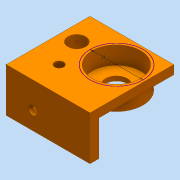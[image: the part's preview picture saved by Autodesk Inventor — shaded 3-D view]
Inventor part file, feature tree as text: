
AUTODESK INVENTOR PART (.ipt)
format: ipt  version: 2016 (Build 200138000, 138)  size: 199,680 bytes
history: native  units: mm
features: extrude x6, sketch x6, hole x5, thicken_offset x2
ambient origin geometry x8: Origin, YZ Plane, XZ Plane, XY Plane, X Axis, Y Axis, Z Axis, Center Point
bodies: Solid1 (feature_tree)
feature tree (19):
  extrude  "Extrusion1"  Depth=20.0mm
  extrude  "Extrusion2"  Depth=16.0mm TaperAngle=0.0deg
  hole  "Hole2"  [1 undecoded]
  hole  "Hole3"  [1 undecoded]
  hole  "Hole4"  [1 undecoded]
  sketch  "Sketch3"  dims[d15=8.0mm d16=8.0mm d17=4.0mm d18=6.0mm d19=8.0mm d20=2.0mm d21=90.0deg d22=8.0mm d23=20.594885mm]
  sketch  "Sketch4"  dims[d24=8.0mm d25=8.0mm d26=4.0mm d27=6.0mm d28=8.0mm d29=2.0mm d30=90.0deg d31=8.0mm d32=20.594885mm]
  sketch  "Sketch5"  dims[d33=8.0mm d34=8.0mm d35=4.0mm d36=6.0mm d37=8.0mm d38=2.0mm d39=90.0deg d40=8.0mm d41=20.594885mm d51=7.0mm]
  extrude  "Extrusion3"  Depth=2.0mm TaperAngle=0.0deg
  extrude  "Extrusion4"  Depth=2.0mm TaperAngle=0.0deg
  extrude  "Extrusion5"  Depth=18.0mm
  sketch  "Sketch6"  dims[d52=7.0mm d53=7.0mm d54=2.0mm d55=0.0mm d56=2.0mm d57=0.0mm d58=2.0mm d59=0.0mm d60=7.0mm d61=25.0mm d62=8.0mm d63=6.0mm d64=4.0mm d65=2.0mm d66=90.0deg d67=8.0mm d68=20.594885mm d80=18.0mm d81=18.0mm d82=18.0mm d83=18.0mm d92=24.0mm d93=10.0mm d94=0.0mm d95=10.0mm d96=6.0mm d97=22.0mm d98=8.0mm d99=90.0deg d100=8.0mm d101=20.594885mm d91=1.0mm]
  thicken_offset  "Thicken3"
  thicken_offset  "Thicken4"
  hole  "Hole5"  [1 undecoded]
  extrude  "Extrusion6"  Depth=18.0mm
  hole  "Hole7"  [1 undecoded]
  sketch  "Sketch1"  dims[d0=20.0mm d1=20.0mm]
  sketch  "Sketch2"  dims[d2=4.0mm d3=0.0mm d4=16.0mm d5=0.0mm]
note: 5 required parameter values undecoded (feature->parameter linkage not recoverable at this tier; creation-order binding heuristic only, values carry confidence <= 0.55)
